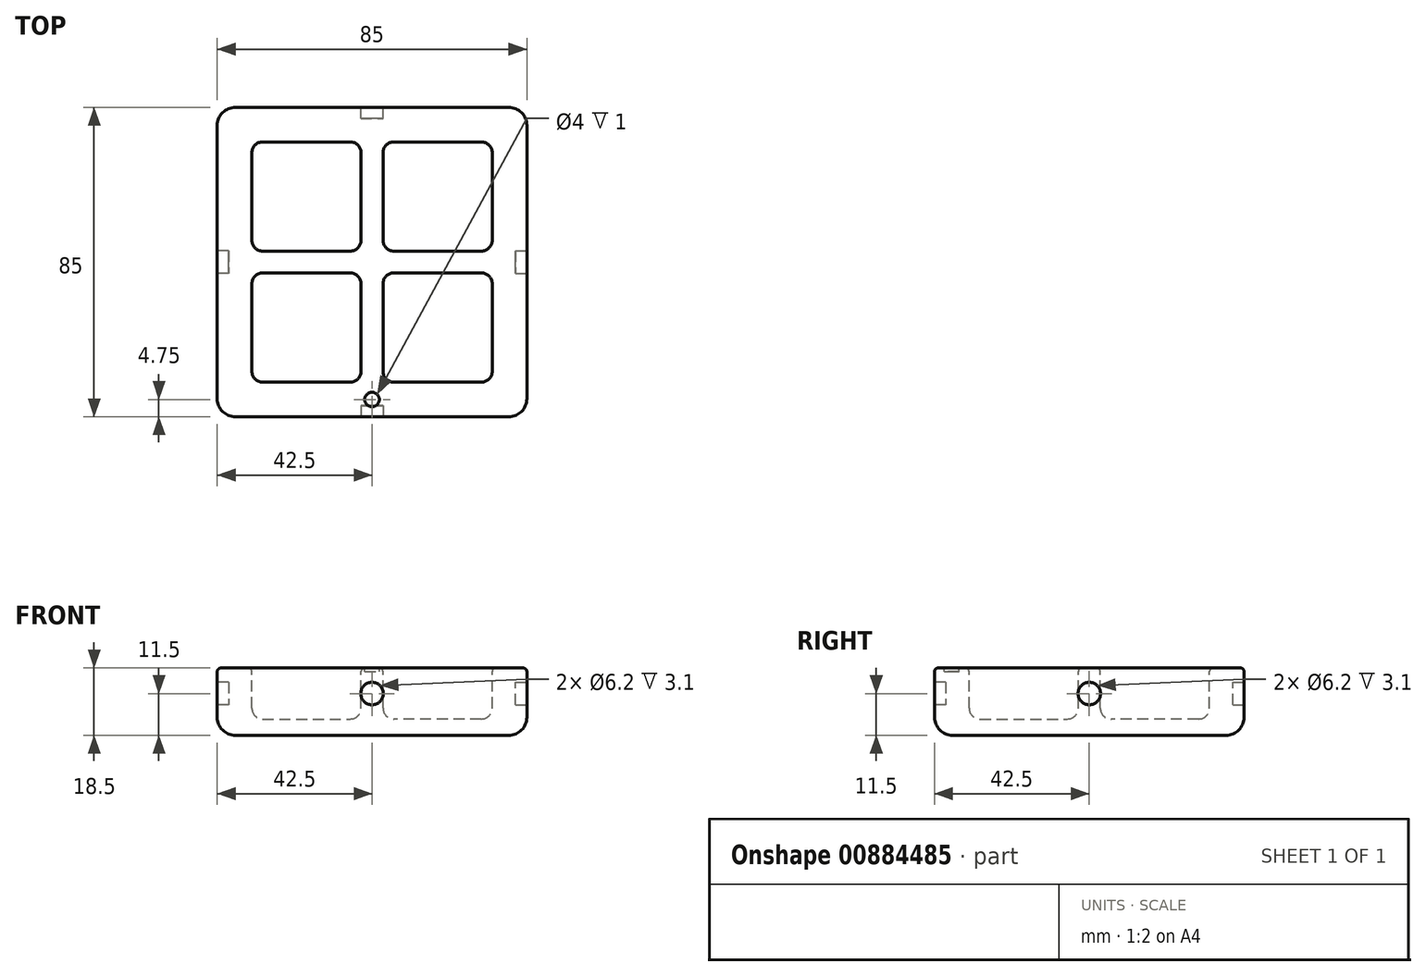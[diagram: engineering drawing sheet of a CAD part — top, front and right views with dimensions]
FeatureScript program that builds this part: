
annotation { "Feature Type Name" : "Feature", "Feature Type Description" : "" }
export const myFeature = defineFeature(function(context is Context, id is Id, definition is map)
    precondition{}
    {
        {
            var Q0;
            Q0=qCreatedBy(makeId("Top.planeOp"),FACE);
            var sketch = newSketch(context, id + "F0", { "sketchPlane" : qUnion([Q0])});
            skLineSegment(sketch, "E0.bottom", {"start": v(-42.5, 42.5) * mm, "end": v(42.5, 42.5) * mm});
            skLineSegment(sketch, "E0.top", {"start": v(-42.5, -42.5) * mm, "end": v(42.5, -42.5) * mm});
            skLineSegment(sketch, "E0.left", {"start": v(-42.5, 42.5) * mm, "end": v(-42.5, -42.5) * mm});
            skLineSegment(sketch, "E0.right", {"start": v(42.5, 42.5) * mm, "end": v(42.5, -42.5) * mm});
            skLineSegment(sketch, "E1.bottom", {"start": v(-30, 33) * mm, "end": v(-6, 33) * mm});
            skLineSegment(sketch, "E1.top", {"start": v(-30, 3) * mm, "end": v(-6, 3) * mm});
            skLineSegment(sketch, "E1.left", {"start": v(-33, 30) * mm, "end": v(-33, 6) * mm});
            skLineSegment(sketch, "E1.right", {"start": v(-3, 30) * mm, "end": v(-3, 6) * mm});
            skLineSegment(sketch, "E2.direction1", {"start": v(-33, 3) * mm, "end": v(-8.24, 3) * mm, "construction": true});
            skPoint(sketch, "E3.visualSharp", {"position": v(-33, 33) * mm});
            skArc(sketch, "E3.filletArc", {"start": v(-30, 33) * mm, "mid": v(-32.12, 32.12) * mm, "end": v(-33, 30) * mm});
            skPoint(sketch, "E4.visualSharp", {"position": v(-3, 33) * mm});
            skArc(sketch, "E4.filletArc", {"start": v(-3, 30) * mm, "mid": v(-3.88, 32.12) * mm, "end": v(-6, 33) * mm});
            skPoint(sketch, "E5.visualSharp", {"position": v(-3, 3) * mm});
            skArc(sketch, "E5.filletArc", {"start": v(-6, 3) * mm, "mid": v(-3.88, 3.88) * mm, "end": v(-3, 6) * mm});
            skPoint(sketch, "E6.visualSharp", {"position": v(-33, 3) * mm});
            skArc(sketch, "E6.filletArc", {"start": v(-33, 6) * mm, "mid": v(-32.12, 3.88) * mm, "end": v(-30, 3) * mm});
            skLineSegment(sketch, "E7.direction1", {"start": v(-33, 3) * mm, "end": v(-6.5, 3) * mm, "construction": true});
            skLineSegment(sketch, "E8", {"start": v(-42.5, 0) * mm, "end": v(42.5, 0) * mm, "construction": true});
            skLineSegment(sketch, "E9", {"start": v(0, -42.5) * mm, "end": v(0, 42.5) * mm, "construction": true});
            skCircle(sketch, "E10", {"center": v(0, -37.75) * mm, "radius": 2 * mm});
            skLineSegment(sketch, "E11.MirrorCS", {"start": v(33, 30) * mm, "end": v(33, 6) * mm});
            skArc(sketch, "E12.MirrorCS", {"start": v(30, 33) * mm, "mid": v(32.12, 32.12) * mm, "end": v(33, 30) * mm});
            skLineSegment(sketch, "E13.MirrorCS", {"start": v(30, 33) * mm, "end": v(6, 33) * mm});
            skArc(sketch, "E14.MirrorCS", {"start": v(3, 30) * mm, "mid": v(3.88, 32.12) * mm, "end": v(6, 33) * mm});
            skLineSegment(sketch, "E15.MirrorCS", {"start": v(3, 30) * mm, "end": v(3, 6) * mm});
            skPoint(sketch, "E16.MirrorP", {"position": v(3, 3) * mm});
            skArc(sketch, "E17.MirrorCS", {"start": v(6, 3) * mm, "mid": v(3.88, 3.88) * mm, "end": v(3, 6) * mm});
            skLineSegment(sketch, "E18.MirrorCS", {"start": v(30, 3) * mm, "end": v(6, 3) * mm});
            skArc(sketch, "E19.MirrorCS", {"start": v(33, 6) * mm, "mid": v(32.12, 3.88) * mm, "end": v(30, 3) * mm});
            skLineSegment(sketch, "E20.MirrorCS", {"start": v(-30, -3) * mm, "end": v(-6, -3) * mm});
            skLineSegment(sketch, "E21.MirrorCS", {"start": v(-30, -33) * mm, "end": v(-6, -33) * mm});
            skLineSegment(sketch, "E22.MirrorCS", {"start": v(-3, -30) * mm, "end": v(-3, -6) * mm});
            skLineSegment(sketch, "E23.MirrorCS", {"start": v(-33, -30) * mm, "end": v(-33, -6) * mm});
            skArc(sketch, "E24.MirrorCS", {"start": v(-33, -6) * mm, "mid": v(-32.12, -3.88) * mm, "end": v(-30, -3) * mm});
            skArc(sketch, "E25.MirrorCS", {"start": v(-6, -3) * mm, "mid": v(-3.88, -3.88) * mm, "end": v(-3, -6) * mm});
            skArc(sketch, "E26.MirrorCS", {"start": v(-3, -30) * mm, "mid": v(-3.88, -32.12) * mm, "end": v(-6, -33) * mm});
            skArc(sketch, "E27.MirrorCS", {"start": v(-30, -33) * mm, "mid": v(-32.12, -32.12) * mm, "end": v(-33, -30) * mm});
            skLineSegment(sketch, "E28.MirrorCS", {"start": v(30, -3) * mm, "end": v(6, -3) * mm});
            skArc(sketch, "E29.MirrorCS", {"start": v(6, -3) * mm, "mid": v(3.88, -3.88) * mm, "end": v(3, -6) * mm});
            skLineSegment(sketch, "E30.MirrorCS", {"start": v(3, -30) * mm, "end": v(3, -6) * mm});
            skArc(sketch, "E31.MirrorCS", {"start": v(3, -30) * mm, "mid": v(3.88, -32.12) * mm, "end": v(6, -33) * mm});
            skArc(sketch, "E32.MirrorCS", {"start": v(30, -33) * mm, "mid": v(32.12, -32.12) * mm, "end": v(33, -30) * mm});
            skLineSegment(sketch, "E33.MirrorCS", {"start": v(33, -30) * mm, "end": v(33, -6) * mm});
            skArc(sketch, "E34.MirrorCS", {"start": v(33, -6) * mm, "mid": v(32.12, -3.88) * mm, "end": v(30, -3) * mm});
            skLineSegment(sketch, "E35.MirrorCS", {"start": v(30, -33) * mm, "end": v(6, -33) * mm});
            skSolve(sketch);
        }
        {
            assignVariable(context, id + "F1", {"name" : "h", "anyValue" : 18.5});
        }
        {
            assignVariable(context, id + "F2", {"name" : "d", "anyValue" : 14});
        }
        {
            var Q0;
            Q0=makeQuery(id+"F0.imprint","IMPRINT",FACE,{"disambiguationData":[TD([[makeQuery(id+"F0.imprint","IMPRINT",EDGE,{"derivedFrom":sQuery(id+"F0.wireOp",EDGE,"E1.bottom")}),-1.0]])]});
            var Q1;
            Q1=makeQuery(id+"F0.imprint","IMPRINT",FACE,{"disambiguationData":[TD([[makeQuery(id+"F0.imprint","IMPRINT",EDGE,{"derivedFrom":sQuery(id+"F0.wireOp",EDGE,"E0.bottom")}),-1.0]])]});
            var Q2;
            Q2=makeQuery(id+"F0.imprint","IMPRINT",FACE,{"disambiguationData":[TD([[makeQuery(id+"F0.imprint","IMPRINT",EDGE,{"derivedFrom":sQuery(id+"F0.wireOp",EDGE,"E10")}),1.0]])]});
            var Q3;
            Q3=makeQuery(id+"F0.imprint","IMPRINT",FACE,{"disambiguationData":[TD([[makeQuery(id+"F0.imprint","IMPRINT",EDGE,{"derivedFrom":sQuery(id+"F0.wireOp",EDGE,"E11.MirrorCS")}),-1.0]])]});
            var Q4;
            Q4=makeQuery(id+"F0.imprint","IMPRINT",FACE,{"disambiguationData":[TD([[makeQuery(id+"F0.imprint","IMPRINT",EDGE,{"derivedFrom":sQuery(id+"F0.wireOp",EDGE,"E28.MirrorCS")}),1.0]])]});
            var Q5;
            Q5=makeQuery(id+"F0.imprint","IMPRINT",FACE,{"disambiguationData":[TD([[makeQuery(id+"F0.imprint","IMPRINT",EDGE,{"derivedFrom":sQuery(id+"F0.wireOp",EDGE,"E20.MirrorCS")}),-1.0]])]});
            extrude(context, id + "F3", {"entities" : qUnion([Q0, Q1, Q2, Q3, Q4, Q5]), "depth" : (getVariable(context, 'h')) * mm, "offsetDistance" : 25 * mm});
        }
        {
            var Q0;
            Q0=makeQuery(id+"F0.imprint","IMPRINT",FACE,{"disambiguationData":[TD([[makeQuery(id+"F0.imprint","IMPRINT",EDGE,{"derivedFrom":sQuery(id+"F0.wireOp",EDGE,"E1.bottom")}),-1.0]])]});
            var Q1;
            Q1=makeQuery(id+"F0.imprint","IMPRINT",FACE,{"disambiguationData":[TD([[makeQuery(id+"F0.imprint","IMPRINT",EDGE,{"derivedFrom":sQuery(id+"F0.wireOp",EDGE,"E20.MirrorCS")}),-1.0]])]});
            var Q2;
            Q2=makeQuery(id+"F0.imprint","IMPRINT",FACE,{"disambiguationData":[TD([[makeQuery(id+"F0.imprint","IMPRINT",EDGE,{"derivedFrom":sQuery(id+"F0.wireOp",EDGE,"E28.MirrorCS")}),1.0]])]});
            var Q3;
            Q3=makeQuery(id+"F0.imprint","IMPRINT",FACE,{"disambiguationData":[TD([[makeQuery(id+"F0.imprint","IMPRINT",EDGE,{"derivedFrom":sQuery(id+"F0.wireOp",EDGE,"E11.MirrorCS")}),-1.0]])]});
            extrude(context, id + "F4", {"entities" : qUnion([Q0, Q1, Q2, Q3]), "operationType" : NewBodyOperationType.REMOVE, "depth" : (getVariable(context, 'd')) * mm, "offsetDistance" : 25 * mm});
        }
        {
            var Q0;
            Q0=makeQuery(id+"F3.opExtrude","CAP_FACE",FACE,{"disambiguationData":[OSD([sQuery(id+"F0.wireOp",EDGE,"E0.bottom"),sQuery(id+"F0.wireOp",EDGE,"E0.top"),sQuery(id+"F0.wireOp",EDGE,"E0.left"),sQuery(id+"F0.wireOp",EDGE,"E0.right")])],"isStart":false});
            var Q1;
            Q1=makeQuery(id+"F3.opExtrude","SWEPT_EDGE",EDGE,{"disambiguationData":[OSD([sQuery(id+"F0.wireOp",EDGE,"E0.bottom"),sQuery(id+"F0.wireOp",EDGE,"E0.right")])]});
            var Q2;
            Q2=makeQuery(id+"F3.opExtrude","SWEPT_EDGE",EDGE,{"disambiguationData":[OSD([sQuery(id+"F0.wireOp",EDGE,"E0.bottom"),sQuery(id+"F0.wireOp",EDGE,"E0.left")])]});
            var Q3;
            Q3=makeQuery(id+"F3.opExtrude","SWEPT_EDGE",EDGE,{"disambiguationData":[OSD([sQuery(id+"F0.wireOp",EDGE,"E0.top"),sQuery(id+"F0.wireOp",EDGE,"E0.left")])]});
            var Q4;
            Q4=makeQuery(id+"F3.opExtrude","SWEPT_EDGE",EDGE,{"disambiguationData":[OSD([sQuery(id+"F0.wireOp",EDGE,"E0.top"),sQuery(id+"F0.wireOp",EDGE,"E0.right")])]});
            fillet(context, id + "F5", {"entities" : qUnion([Q0, Q1, Q2, Q3, Q4]), "radius" : 5 * mm, "tangentPropagation" : true, "allowEdgeOverflow" : false});
        }
        {
            var Q0;
            Q0=makeQuery(id+"F4.boolean.opBoolean","COPY",FACE,{"derivedFrom":makeQuery(id+"F4.opExtrude","CAP_FACE",FACE,{"disambiguationData":[OSD([sQuery(id+"F0.wireOp",EDGE,"E1.bottom"),sQuery(id+"F0.wireOp",EDGE,"E1.top"),sQuery(id+"F0.wireOp",EDGE,"E1.left"),sQuery(id+"F0.wireOp",EDGE,"E1.right"),sQuery(id+"F0.wireOp",EDGE,"E3.filletArc"),sQuery(id+"F0.wireOp",EDGE,"E4.filletArc"),sQuery(id+"F0.wireOp",EDGE,"E5.filletArc"),sQuery(id+"F0.wireOp",EDGE,"E6.filletArc")])],"isStart":false})});
            var Q1;
            Q1=makeQuery(id+"F4.boolean.opBoolean","COPY",FACE,{"derivedFrom":makeQuery(id+"F4.opExtrude","CAP_FACE",FACE,{"disambiguationData":[OSD([sQuery(id+"F0.wireOp",EDGE,"E20.MirrorCS"),sQuery(id+"F0.wireOp",EDGE,"E21.MirrorCS"),sQuery(id+"F0.wireOp",EDGE,"E22.MirrorCS"),sQuery(id+"F0.wireOp",EDGE,"E23.MirrorCS"),sQuery(id+"F0.wireOp",EDGE,"E24.MirrorCS"),sQuery(id+"F0.wireOp",EDGE,"E25.MirrorCS"),sQuery(id+"F0.wireOp",EDGE,"E26.MirrorCS"),sQuery(id+"F0.wireOp",EDGE,"E27.MirrorCS")])],"isStart":false})});
            var Q2;
            Q2=makeQuery(id+"F4.boolean.opBoolean","COPY",FACE,{"derivedFrom":makeQuery(id+"F4.opExtrude","CAP_FACE",FACE,{"disambiguationData":[OSD([sQuery(id+"F0.wireOp",EDGE,"E28.MirrorCS"),sQuery(id+"F0.wireOp",EDGE,"E29.MirrorCS"),sQuery(id+"F0.wireOp",EDGE,"E30.MirrorCS"),sQuery(id+"F0.wireOp",EDGE,"E31.MirrorCS"),sQuery(id+"F0.wireOp",EDGE,"E32.MirrorCS"),sQuery(id+"F0.wireOp",EDGE,"E33.MirrorCS"),sQuery(id+"F0.wireOp",EDGE,"E34.MirrorCS"),sQuery(id+"F0.wireOp",EDGE,"E35.MirrorCS")])],"isStart":false})});
            var Q3;
            Q3=makeQuery(id+"F4.boolean.opBoolean","COPY",FACE,{"derivedFrom":makeQuery(id+"F4.opExtrude","CAP_FACE",FACE,{"disambiguationData":[OSD([sQuery(id+"F0.wireOp",EDGE,"E11.MirrorCS"),sQuery(id+"F0.wireOp",EDGE,"E12.MirrorCS"),sQuery(id+"F0.wireOp",EDGE,"E13.MirrorCS"),sQuery(id+"F0.wireOp",EDGE,"E14.MirrorCS"),sQuery(id+"F0.wireOp",EDGE,"E15.MirrorCS"),sQuery(id+"F0.wireOp",EDGE,"E17.MirrorCS"),sQuery(id+"F0.wireOp",EDGE,"E18.MirrorCS"),sQuery(id+"F0.wireOp",EDGE,"E19.MirrorCS")])],"isStart":false})});
            fillet(context, id + "F6", {"entities" : qUnion([Q0, Q1, Q2, Q3]), "radius" : 3 * mm, "tangentPropagation" : true, "allowEdgeOverflow" : false});
        }
        {
            var Q0;
            Q0=makeQuery(id+"F3.opExtrude","CAP_FACE",FACE,{"disambiguationData":[OSD([sQuery(id+"F0.wireOp",EDGE,"E0.bottom"),sQuery(id+"F0.wireOp",EDGE,"E0.top"),sQuery(id+"F0.wireOp",EDGE,"E0.left"),sQuery(id+"F0.wireOp",EDGE,"E0.right")])],"isStart":true});
            fillet(context, id + "F7", {"entities" : qUnion([Q0]), "radius" : 1 * mm, "tangentPropagation" : true, "allowEdgeOverflow" : false});
        }
        {
            var Q0;
            Q0=makeQuery(id+"F3.opExtrude","SWEPT_FACE",FACE,{"disambiguationData":[OSD([sQuery(id+"F0.wireOp",EDGE,"E0.top")])]});
            var sketch = newSketch(context, id + "F8", { "sketchPlane" : qUnion([Q0])});
            skCircle(sketch, "E36", {"center": v(0, 7) * mm, "radius": 3.1 * mm});
            skSolve(sketch);
        }
        {
            var Q0;
            Q0=makeQuery(id+"F8.imprint","IMPRINT",FACE,{"disambiguationData":[TD([[makeQuery(id+"F8.imprint","IMPRINT",EDGE,{"derivedFrom":sQuery(id+"F8.wireOp",EDGE,"E36")}),1.0]])]});
            extrude(context, id + "F9", {"entities" : qUnion([Q0]), "operationType" : NewBodyOperationType.REMOVE, "oppositeDirection" : true, "depth" : 3.1 * mm, "offsetDistance" : 25 * mm});
        }
        {
            var Q0;
            Q0=makeQuery(id+"F3.opExtrude","SWEPT_FACE",FACE,{"disambiguationData":[OSD([sQuery(id+"F0.wireOp",EDGE,"E0.bottom")])]});
            var sketch = newSketch(context, id + "F10", { "sketchPlane" : qUnion([Q0])});
            skCircle(sketch, "E37", {"center": v(0, 7) * mm, "radius": 3.1 * mm});
            skSolve(sketch);
        }
        {
            var Q0;
            Q0=makeQuery(id+"F10.imprint","IMPRINT",FACE,{"disambiguationData":[TD([[makeQuery(id+"F10.imprint","IMPRINT",EDGE,{"derivedFrom":sQuery(id+"F10.wireOp",EDGE,"E37")}),1.0]])]});
            extrude(context, id + "F11", {"entities" : qUnion([Q0]), "operationType" : NewBodyOperationType.REMOVE, "oppositeDirection" : true, "depth" : 3.1 * mm, "offsetDistance" : 25 * mm});
        }
        {
            var Q0;
            Q0=makeQuery(id+"F3.opExtrude","SWEPT_FACE",FACE,{"disambiguationData":[OSD([sQuery(id+"F0.wireOp",EDGE,"E0.left")])]});
            var sketch = newSketch(context, id + "F12", { "sketchPlane" : qUnion([Q0])});
            skCircle(sketch, "E38", {"center": v(0, 7) * mm, "radius": 3.1 * mm});
            skSolve(sketch);
        }
        {
            var Q0;
            Q0=makeQuery(id+"F12.imprint","IMPRINT",FACE,{"disambiguationData":[TD([[makeQuery(id+"F12.imprint","IMPRINT",EDGE,{"derivedFrom":sQuery(id+"F12.wireOp",EDGE,"E38")}),1.0]])]});
            extrude(context, id + "F13", {"entities" : qUnion([Q0]), "operationType" : NewBodyOperationType.REMOVE, "oppositeDirection" : true, "depth" : 3.1 * mm, "offsetDistance" : 25 * mm});
        }
        {
            var Q0;
            Q0=makeQuery(id+"F3.opExtrude","SWEPT_FACE",FACE,{"disambiguationData":[OSD([sQuery(id+"F0.wireOp",EDGE,"E0.right")])]});
            var sketch = newSketch(context, id + "F14", { "sketchPlane" : qUnion([Q0])});
            skCircle(sketch, "E39", {"center": v(0, 7) * mm, "radius": 3.1 * mm});
            skSolve(sketch);
        }
        {
            var Q0;
            Q0=makeQuery(id+"F14.imprint","IMPRINT",FACE,{"disambiguationData":[TD([[makeQuery(id+"F14.imprint","IMPRINT",EDGE,{"derivedFrom":sQuery(id+"F14.wireOp",EDGE,"E39")}),1.0]])]});
            extrude(context, id + "F15", {"entities" : qUnion([Q0]), "operationType" : NewBodyOperationType.REMOVE, "oppositeDirection" : true, "depth" : 3.1 * mm, "offsetDistance" : 25 * mm});
        }
        {
            var Q0;
            Q0=makeQuery(id+"F0.imprint","IMPRINT",FACE,{"disambiguationData":[TD([[makeQuery(id+"F0.imprint","IMPRINT",EDGE,{"derivedFrom":sQuery(id+"F0.wireOp",EDGE,"E10")}),1.0]])]});
            var Q1;
            Q1=sQuery(id+"F0.wireOp",EDGE,"E10");
            extrude(context, id + "F16", {"entities" : qUnion([Q0]), "operationType" : NewBodyOperationType.REMOVE, "surfaceEntities" : qUnion([Q1]), "depth" : 1 * mm, "offsetDistance" : 25 * mm});
        }
        {
            var Q0;
            Q0=makeQuery(id+"F3.opExtrude","SWEPT_BODY",BODY,{"disambiguationData":[OSD([sQuery(id+"F0.wireOp",EDGE,"E0.bottom"),sQuery(id+"F0.wireOp",EDGE,"E0.top"),sQuery(id+"F0.wireOp",EDGE,"E0.left"),sQuery(id+"F0.wireOp",EDGE,"E0.right")])]});
            var Q1;
            Q1=sQuery(id+"F0.wireOp",EDGE,"E9");
            transform(context, id + "F17", {"entities" : qUnion([Q0]), "transformType" : TransformType.ROTATION, "transformAxis" : qUnion([Q1]), "angle" : 180 * degree, "makeCopy" : false});
        }
    });
